# Revit family: 2071453
name_source: partatom
category: Lighting Fixtures
units: mm (PartAtom-declared; Revit-internal decimal feet)

## family parameters
Cut with Voids When Loaded = No
Host = Face
Light Source = Yes
Maintain Annotation Orientation = No
OmniClass Number = 23.80.70.00
OmniClass Title = Lighting
Part Type = Normal
Room Calculation Point = No
Round Connector Dimension = Use Diameter
Shared = No

## types (1)
- MC2 D/I 1.2M 4K DALI WHT PRIS
    Apparent Load = 31 VA
    Assembly Code = D5020200
    AssetType = Fixed
    ClassificationName = Uniclass2015
    ClassificationValue = EF_70_80
    Color Filter = 16777215
    Cost = 0 $
    Default Elevation = 1219 mm
    Description = MC2 D/I 1.2M 4K DALI WHT PRIS LED luminaire, white RAL9016 finishing, direct/indirect distribution (65/35), various accessories available, compact and minimalist design based on the Golden Mean, ideal for offices, meeting rooms, corridors, education facilities, museums and libraries, extruded aluminium body, diffuser: micro prismatic, colour temperature: 4000K neutral white, total system power: 29W, total fixture output: 3850lm, luminaire efficacy: 133lm/W, LOR: 100%, colour rendering: Ra >80, LED Chromacity: 3 step MacAdam ellipse, lifespan: 66,000 hours L90B10, IR/UV free light source without heat radiation, operating voltage: 220-240V / 50-60Hz, drive current: (Direct) 800mA + (Indirect) 350mA, electronic driver, DALI dimmable, direct/indirect independently addressable, electrical protection: CLASS I, ingress protection rating: IP20, suitable for internal environment only.
    Dimming Lamp Color Temperature Shift = <None>
    DimmingControlOptions = DALI
    DocumentationLiterature = https://www.sylvania-lighting.com
    ElectricShockClassification = Class I
    EmergencyLight = No
    Emit Shape Visible in Rendering = No
    Emit from Rectangle Length = 1200 mm  [stored 3.93701 ft]
    Emit from Rectangle Width = 54 mm  [stored 0.177165 ft]
    IfcExportAs = IfcLightFixtureType
    IfcExportType = IfcLightFixtureType
    ImpactProtectionIndex = IK03
    IngressProtection = IP20
    InputNominalFrequency = 50/60Hz
    InputVoltage = 220-240 V
    Keynote = 16500
    Lamp = LED
    LampColourRenderingIndex = 80
    LampColourTemperature = 4000 K
    LampMacAdamStep = 3
    LampNominalLuminous = 3850 lm
    LampsType = LED
    LightOutputRatio = 100
    LuminaireType = Suspended
    LuminousEfficacy = 133 lm/W
    Manufacturer = Feilo Sylvania
    ManufacturerName = Feilo Sylvania
    Material = Aluminium
    Material_1_SYL = Metal_Sylvania_Mini Continuum II_White
    Material_2_SYL = Polycarbonate_Sylvania_Mini Continuum II_Prismatic_4000K
    Material_3_SYL = Metal_Sylvania_Mini Contiuum II_Silver
    Material_4_SYL = <By Category>
    Model = MC2 D/I 1.2M 4K DALI WHT PRIS
    ModelNumber = 2071453
    ModelReference = MC2 D/I 1.2M 4K DALI WHT PRIS
    Name = MC2 D/I 1.2M 4K DALI WHT PRIS
    NominalDepth = 54 mm  [stored 0.177165 ft]
    NominalHeight = 86 mm  [stored 0.282152 ft]
    NominalLength = 1200 mm  [stored 3.93701 ft]
    PendantMax = 3000 mm  [stored 9.84252 ft]
    PendantMin = 50 mm  [stored 0.164042 ft]
    Photometric Web File = 2071453.ies
    PowerConsumption = 29 W
    PowerFactor = 0.95
    SuspensionDistance1 = 62 mm  [stored 0.203412 ft]
    SuspensionDistance2 = 82 mm  [stored 0.269029 ft]
    Tilt Angle = -90.00°
    Type Image = <None>
    TypeName = Mini Continuum II - Direct/Indirect
    URL = http://www.sylvania-group.com
    Voltage = 230 V
    WarrantyDescription = http://www.sylvania-group.com
    WarrantyDurationParts = 5
    WarrantyDurationUnit = Years
    Weight = 3.1 kg

note: [stored X ft] marks values corroborated as IEEE doubles in the binary element streams (Revit-internal decimal feet)

## geometry (parser evidence)
native form markers: Sweep x2
no freeform markers — native parametric forms only
